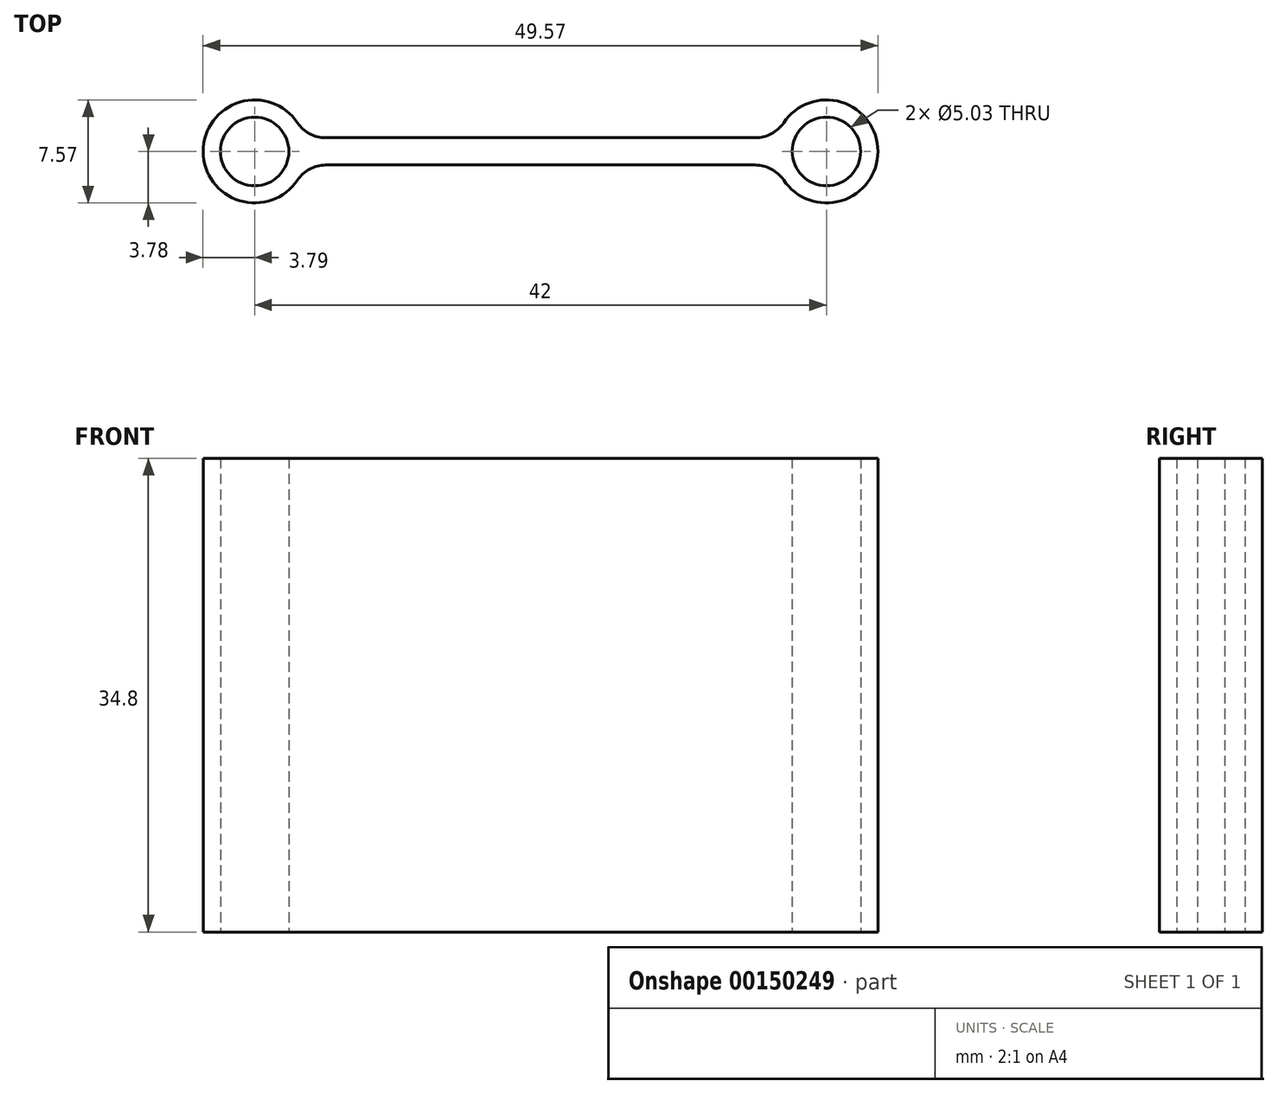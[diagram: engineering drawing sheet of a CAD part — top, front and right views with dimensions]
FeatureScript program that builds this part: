
annotation { "Feature Type Name" : "Feature", "Feature Type Description" : "" }
export const myFeature = defineFeature(function(context is Context, id is Id, definition is map)
    precondition{}
    {
        {
            var Q0;
            Q0=qCreatedBy(makeId("Top.planeOp"),FACE);
            var sketch = newSketch(context, id + "F0", { "sketchPlane" : qUnion([Q0])});
            skCircle(sketch, "E0", {"center": v(-21, 0) * mm, "radius": 2.52 * mm});
            skCircle(sketch, "E1", {"center": v(21, 0) * mm, "radius": 2.52 * mm});
            skLineSegment(sketch, "E2", {"start": v(-15.78, 1) * mm, "end": v(15.78, 1) * mm});
            skLineSegment(sketch, "E3", {"start": v(-15.78, -1) * mm, "end": v(15.78, -1) * mm});
            skArc(sketch, "E4", {"start": v(-17.86, 2.1) * mm, "mid": v(-24.79, 0) * mm, "end": v(-17.86, -2.1) * mm});
            skArc(sketch, "E5", {"start": v(17.86, -2.1) * mm, "mid": v(24.78, 0) * mm, "end": v(17.86, 2.1) * mm});
            skPoint(sketch, "E6.visualSharp", {"position": v(-17.35, 1) * mm});
            skArc(sketch, "E6.filletArc", {"start": v(-17.86, 2.1) * mm, "mid": v(-16.96, 1.3) * mm, "end": v(-15.78, 1) * mm});
            skPoint(sketch, "E7.visualSharp", {"position": v(-17.35, -1) * mm});
            skArc(sketch, "E7.filletArc", {"start": v(-15.78, -1) * mm, "mid": v(-16.96, -1.3) * mm, "end": v(-17.86, -2.1) * mm});
            skPoint(sketch, "E8.visualSharp", {"position": v(17.35, 1) * mm});
            skArc(sketch, "E8.filletArc", {"start": v(15.78, 1) * mm, "mid": v(16.96, 1.3) * mm, "end": v(17.86, 2.1) * mm});
            skPoint(sketch, "E9.visualSharp", {"position": v(17.35, -1) * mm});
            skArc(sketch, "E9.filletArc", {"start": v(17.86, -2.1) * mm, "mid": v(16.96, -1.3) * mm, "end": v(15.78, -1) * mm});
            skSolve(sketch);
        }
        {
            var Q0;
            Q0=qSketchRegion(id+"F0",true);
            extrude(context, id + "F1", {"entities" : qUnion([Q0]), "depth" : 34.8 * mm});
        }
    });
